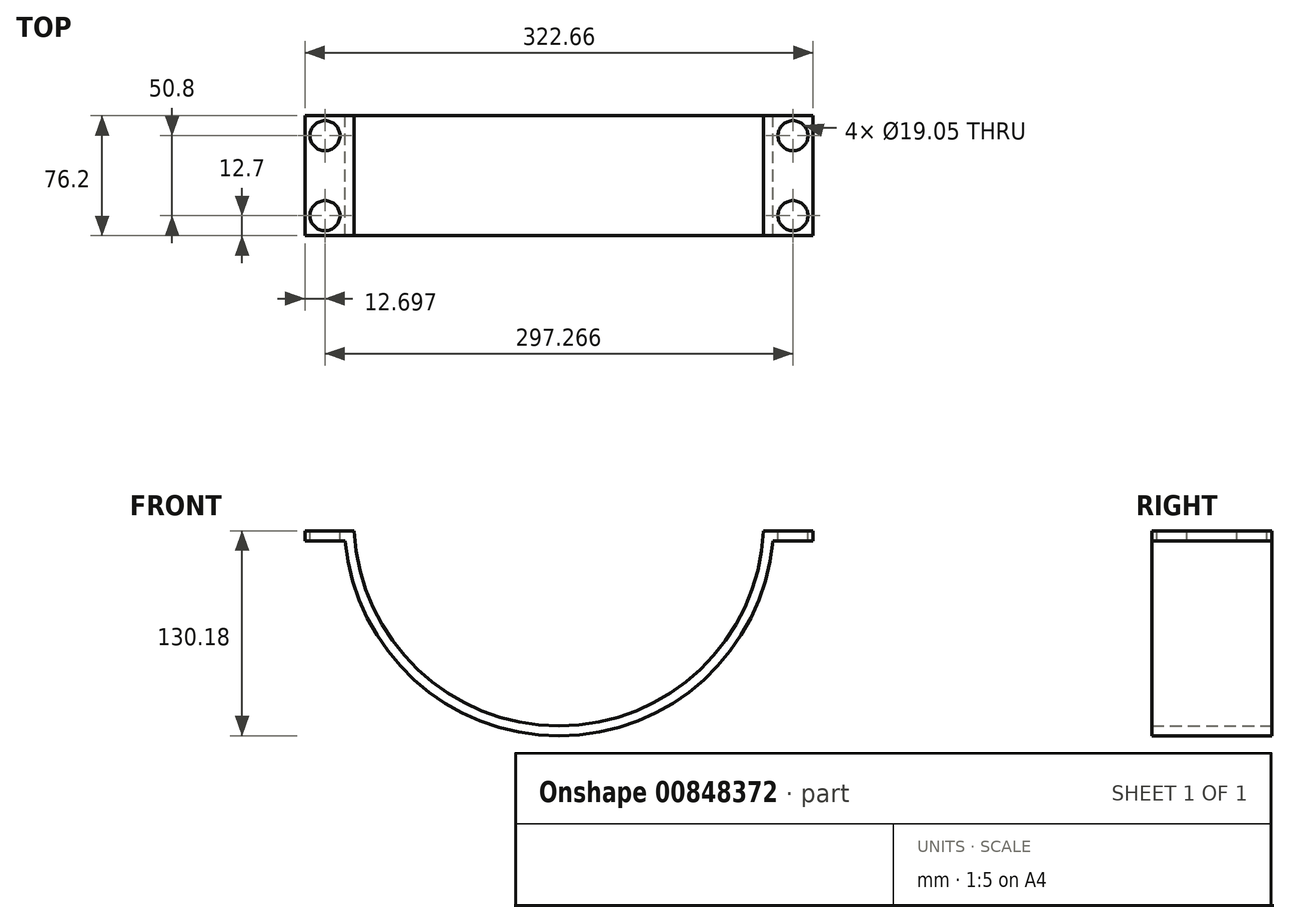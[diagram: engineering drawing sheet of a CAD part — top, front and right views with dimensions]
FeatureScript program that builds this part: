
annotation { "Feature Type Name" : "Feature", "Feature Type Description" : "" }
export const myFeature = defineFeature(function(context is Context, id is Id, definition is map)
    precondition{}
    {
        {
            var Q0;
            Q0=qCreatedBy(makeId("Front.planeOp"),FACE);
            var sketch = newSketch(context, id + "F0", { "sketchPlane" : qUnion([Q0])});
            skArc(sketch, "E0", {"start": v(-135.93, -6.35) * mm, "mid": v(0, -130.18) * mm, "end": v(135.93, -6.35) * mm});
            skArc(sketch, "E1", {"start": v(-130.02, 0) * mm, "mid": v(0, -123.83) * mm, "end": v(130.02, 0) * mm});
            skLineSegment(sketch, "E2", {"start": v(-130.02, 0) * mm, "end": v(-161.33, 0) * mm});
            skLineSegment(sketch, "E3", {"start": v(-161.33, 0) * mm, "end": v(-161.33, -6.35) * mm});
            skLineSegment(sketch, "E4", {"start": v(-161.33, -6.35) * mm, "end": v(-135.93, -6.35) * mm});
            skLineSegment(sketch, "E5", {"start": v(130.02, 0) * mm, "end": v(161.33, 0) * mm});
            skLineSegment(sketch, "E6", {"start": v(161.33, 0) * mm, "end": v(161.33, -6.35) * mm});
            skLineSegment(sketch, "E7", {"start": v(161.33, -6.35) * mm, "end": v(135.93, -6.35) * mm});
            skSolve(sketch);
        }
        {
            var Q0;
            Q0 = qSketchRegion(id + "F0", true);
            extrude(context, id + "F1", {"entities" : qUnion([Q0]), "depth" : 76.2 * mm, "offsetDistance" : 25.4 * mm});
        }
        {
            var Q0;
            Q0=makeQuery(id+"F1.opExtrude","SWEPT_FACE",FACE,{"disambiguationData":[OSD([sQuery(id+"F0.wireOp",EDGE,"E2")])]});
            var sketch = newSketch(context, id + "F2", { "sketchPlane" : qUnion([Q0])});
            skPoint(sketch, "E8", {"position": v(-148.63, -63.5) * mm});
            skPoint(sketch, "E9", {"position": v(-148.63, -12.7) * mm});
            skPoint(sketch, "E10", {"position": v(148.63, -63.5) * mm});
            skPoint(sketch, "E11", {"position": v(148.63, -12.7) * mm});
            skLineSegment(sketch, "E12", {"start": v(-161.33, -38.1) * mm, "end": v(120.6, -38.1) * mm, "construction": true});
            skSolve(sketch);
        }
        {
            var Q0;
            Q0=sQuery(id+"F2.wireOp",VERTEX,"E8");
            var Q1;
            Q1=sQuery(id+"F2.wireOp",VERTEX,"E9");
            var Q2;
            Q2=sQuery(id+"F2.wireOp",VERTEX,"E10");
            var Q3;
            Q3=sQuery(id+"F2.wireOp",VERTEX,"E11");
            var Q4;
            Q4=makeQuery(id+"F1.opExtrude","SWEPT_BODY",BODY,{"disambiguationData":[OSD([sQuery(id+"F0.wireOp",EDGE,"E0"),sQuery(id+"F0.wireOp",EDGE,"E1"),sQuery(id+"F0.wireOp",EDGE,"E2"),sQuery(id+"F0.wireOp",EDGE,"E3"),sQuery(id+"F0.wireOp",EDGE,"E4"),sQuery(id+"F0.wireOp",EDGE,"E5"),sQuery(id+"F0.wireOp",EDGE,"E6"),sQuery(id+"F0.wireOp",EDGE,"E7")])]});
            hole(context, id + "F3", {"style" : HoleStyle.SIMPLE, "endStyle" : HoleEndStyle.THROUGH, "holeDiameter" : 19.05 * mm, "majorDiameter" : 6.35 * mm, "isTappedThrough" : true, "tappedDepth" : 12.7 * mm, "tapClearance" : 3, "locations" : qUnion([Q0, Q1, Q2, Q3]), "scope" : qUnion([Q4])});
        }
    });
